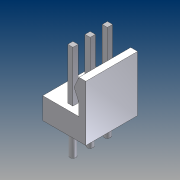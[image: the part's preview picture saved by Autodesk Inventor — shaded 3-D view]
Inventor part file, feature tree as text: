
AUTODESK INVENTOR PART (.ipt)
format: ipt  version: 2012 (Build 160160000, 160)  size: 118,272 bytes
history: native  units: mm (DEFAULTED — no unit token found)
features: extrude x3, plane x3, sketch x2, pattern_linear x1
ambient origin geometry x5: Origin, X Axis, Y Axis, Z Axis, Center Point
bodies: Solid1 (feature_tree)
feature tree (9):
  extrude  "Extrusion1"  Depth=3.175mm
  sketch  "Sketch3"  dims[d2=8.1788mm d3=1.4478mm d4=1.016mm d5=2.54mm d6=0.0mm d7=0.762mm d8=3.556mm d9=0.0mm d10=10.668mm d11=0.0mm d12=30.0mm d14=2.54mm d15=0.889mm]
  extrude  "Extrusion2"  Depth=1.4478mm
  extrude  "Extrusion3"  Depth=1.016mm
  pattern_linear  "Rectangular Pattern1"  Spacing1=2.54mm  [1 undecoded]
  plane  "YZ Plane (RIGHT)"
  plane  "XZ Plane (TOP)"
  plane  "XY Plane (FRONT)"
  sketch  "Sketch2"  dims[d0=6.35mm d1=3.175mm]
note: 1 required parameter value undecoded (feature->parameter linkage not recoverable at this tier; creation-order binding heuristic only, values carry confidence <= 0.55)
